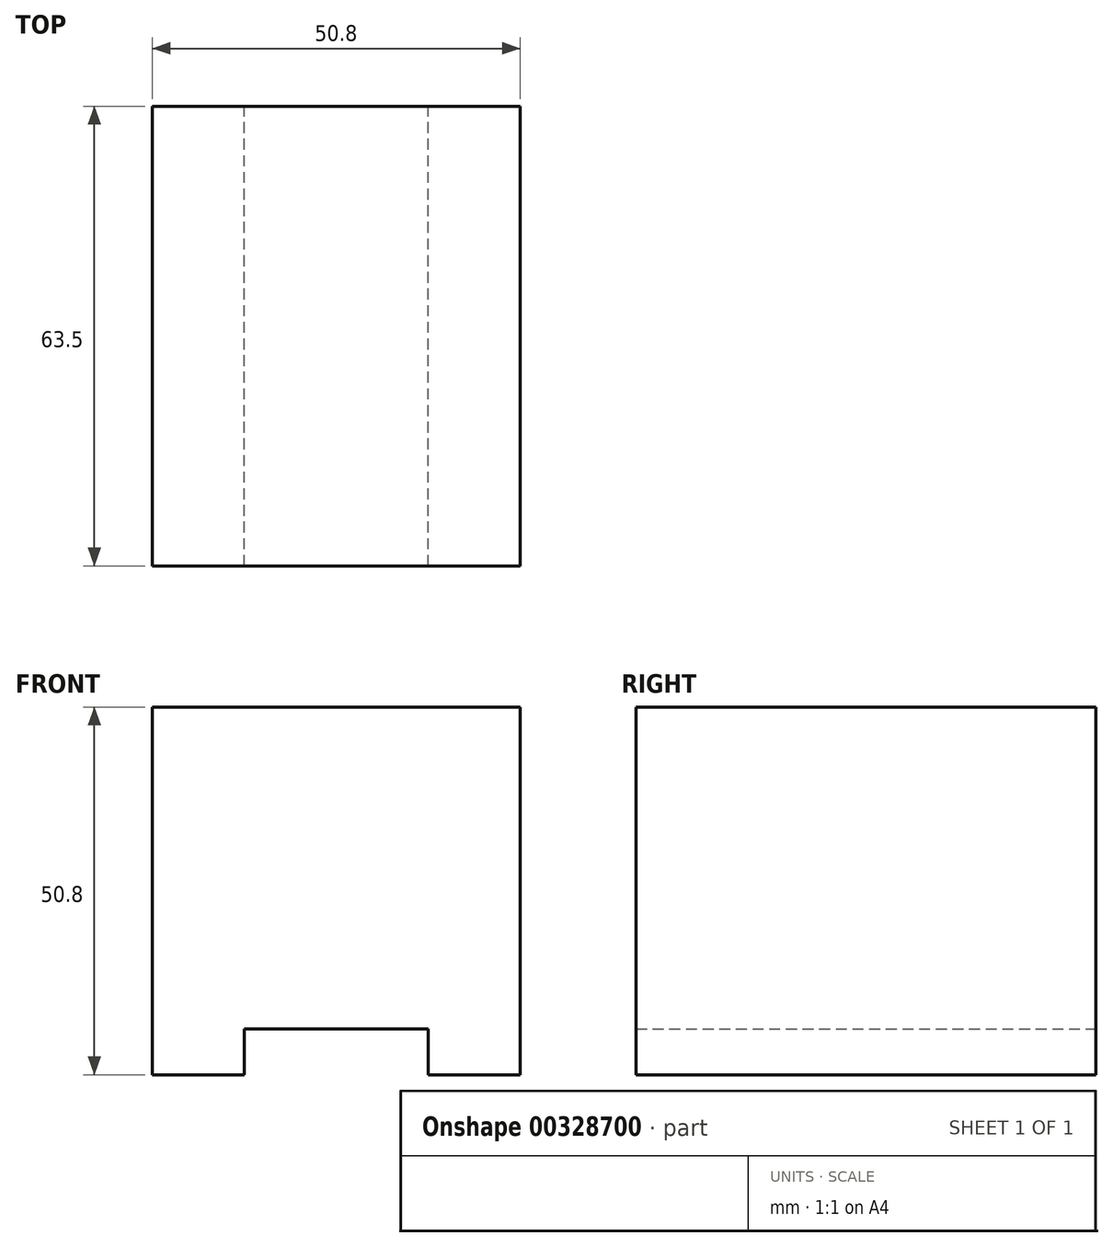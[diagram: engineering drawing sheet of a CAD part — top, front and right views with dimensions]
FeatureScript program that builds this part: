
annotation { "Feature Type Name" : "Feature", "Feature Type Description" : "" }
export const myFeature = defineFeature(function(context is Context, id is Id, definition is map)
    precondition{}
    {
        {
            var Q0;
            Q0=qCreatedBy(makeId("Front.planeOp"),FACE);
            var sketch = newSketch(context, id + "F0", { "sketchPlane" : qUnion([Q0])});
            skPoint(sketch, "E0.middle", {"position": v(0, 0) * mm});
            skLineSegment(sketch, "E1.0", {"start": v(25.4, -25.4) * mm, "end": v(12.7, -25.4) * mm});
            skLineSegment(sketch, "E1.1", {"start": v(25.4, -25.4) * mm, "end": v(25.4, 25.4) * mm});
            skLineSegment(sketch, "E1.2", {"start": v(25.4, 25.4) * mm, "end": v(-25.4, 25.4) * mm});
            skLineSegment(sketch, "E1.3", {"start": v(-25.4, -25.4) * mm, "end": v(-25.4, 25.4) * mm});
            skLineSegment(sketch, "E2.0", {"start": v(-12.7, -25.4) * mm, "end": v(-12.7, -19.05) * mm});
            skLineSegment(sketch, "E3.0", {"start": v(12.7, -25.4) * mm, "end": v(12.7, -19.05) * mm});
            skLineSegment(sketch, "E4.0", {"start": v(12.7, -19.05) * mm, "end": v(-12.7, -19.05) * mm});
            skLineSegment(sketch, "E5.trimOffspring", {"start": v(-12.7, -25.4) * mm, "end": v(-25.4, -25.4) * mm});
            skSolve(sketch);
        }
        {
            var Q0;
            Q0 = qSketchRegion(id + "F0", true);
            extrude(context, id + "F1", {"entities" : qUnion([Q0]), "depth" : 63.5 * mm});
        }
    });
